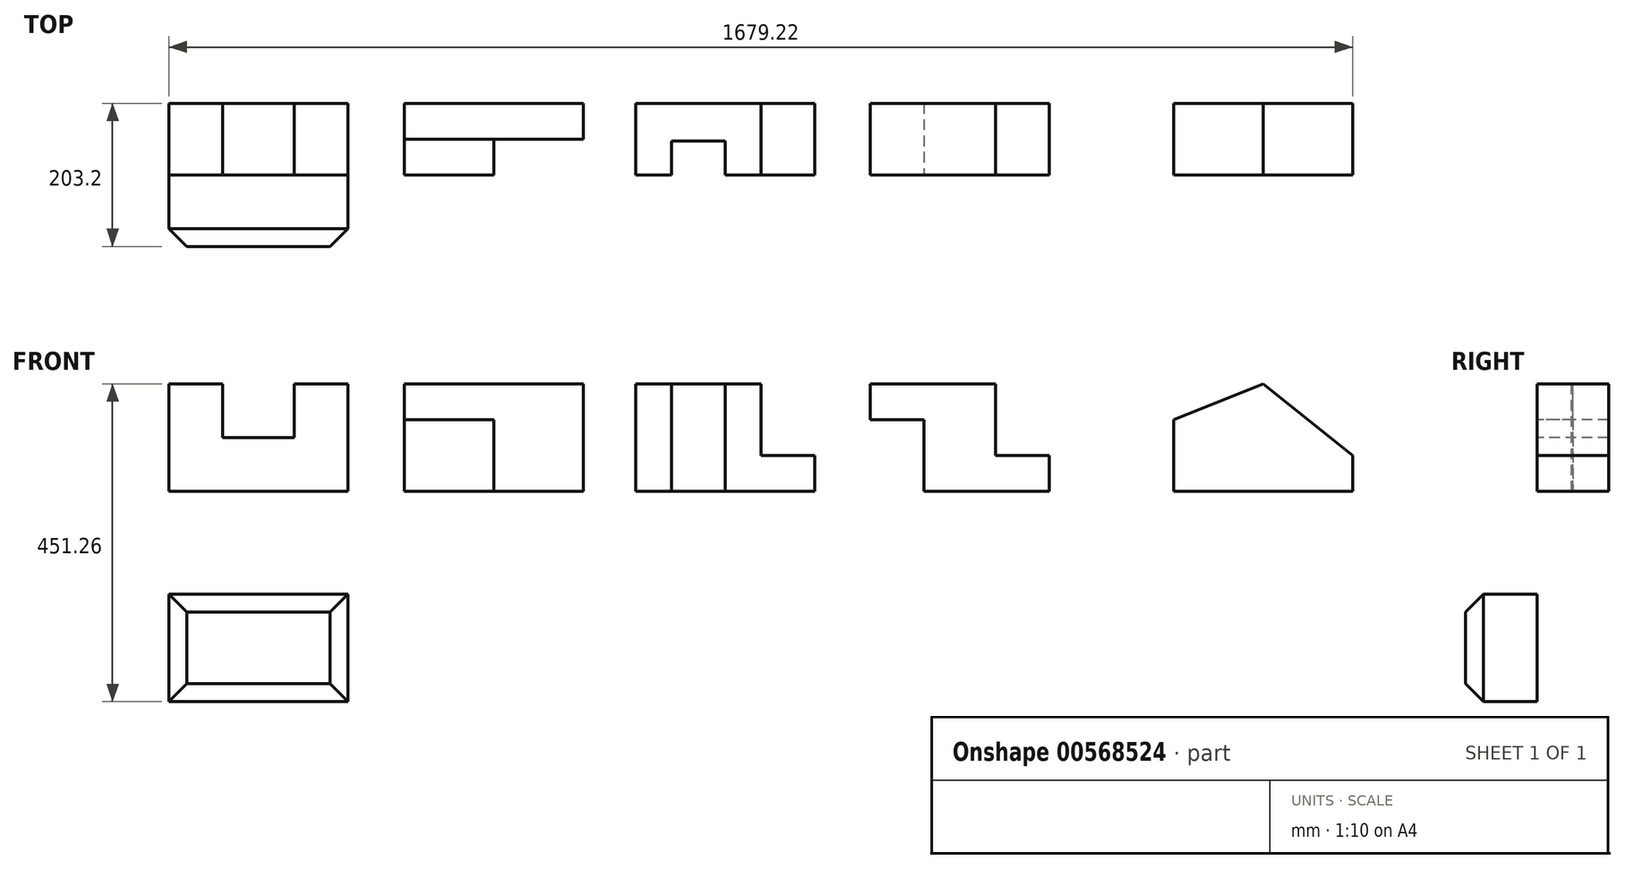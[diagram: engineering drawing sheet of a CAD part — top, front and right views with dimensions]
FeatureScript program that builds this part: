
annotation { "Feature Type Name" : "Feature", "Feature Type Description" : "" }
export const myFeature = defineFeature(function(context is Context, id is Id, definition is map)
    precondition{}
    {
        {
            var Q0;
            Q0=qCreatedBy(makeId("Front.planeOp"),FACE);
            var sketch = newSketch(context, id + "F0", { "sketchPlane" : qUnion([Q0])});
            skLineSegment(sketch, "E0", {"start": v(0, 0) * mm, "end": v(254, 0) * mm});
            skLineSegment(sketch, "E1", {"start": v(254, 0) * mm, "end": v(254, 152.4) * mm});
            skLineSegment(sketch, "E2", {"start": v(254, 152.4) * mm, "end": v(177.8, 152.4) * mm});
            skLineSegment(sketch, "E3", {"start": v(177.8, 152.4) * mm, "end": v(177.8, 76.2) * mm});
            skLineSegment(sketch, "E4", {"start": v(177.8, 76.2) * mm, "end": v(76.2, 76.2) * mm});
            skLineSegment(sketch, "E5", {"start": v(76.2, 76.2) * mm, "end": v(76.2, 152.4) * mm});
            skLineSegment(sketch, "E6", {"start": v(0, 152.4) * mm, "end": v(0, 0) * mm});
            skLineSegment(sketch, "E7", {"start": v(0, 152.4) * mm, "end": v(76.2, 152.4) * mm});
            skSolve(sketch);
        }
        {
            var Q0;
            Q0=makeQuery(id+"F0.imprint","IMPRINT",FACE,{"disambiguationData":[TD([[makeQuery(id+"F0.imprint","IMPRINT",EDGE,{"derivedFrom":sQuery(id+"F0.wireOp",EDGE,"E0")}),1.0]])]});
            extrude(context, id + "F1", {"entities" : qUnion([Q0]), "oppositeDirection" : true, "depth" : 101.6 * mm, "offsetDistance" : 25.4 * mm});
        }
        {
            var Q0;
            Q0=qCreatedBy(makeId("Front.planeOp"),FACE);
            var sketch = newSketch(context, id + "F2", { "sketchPlane" : qUnion([Q0])});
            skLineSegment(sketch, "E8.bottom", {"start": v(334.13, 0) * mm, "end": v(588.13, 0) * mm});
            skLineSegment(sketch, "E8.top", {"start": v(334.13, 152.4) * mm, "end": v(588.13, 152.4) * mm});
            skLineSegment(sketch, "E8.left", {"start": v(334.13, 0) * mm, "end": v(334.13, 152.4) * mm});
            skLineSegment(sketch, "E8.right", {"start": v(588.13, 0) * mm, "end": v(588.13, 152.4) * mm});
            skSolve(sketch);
        }
        {
            var Q0;
            Q0=makeQuery(id+"F2.imprint","IMPRINT",FACE,{"disambiguationData":[TD([[makeQuery(id+"F2.imprint","IMPRINT",EDGE,{"derivedFrom":sQuery(id+"F2.wireOp",EDGE,"E8.bottom")}),1.0]])]});
            extrude(context, id + "F3", {"entities" : qUnion([Q0]), "oppositeDirection" : true, "depth" : 101.6 * mm, "offsetDistance" : 25.4 * mm});
        }
        {
            var Q0;
            Q0=makeQuery(id+"F3.opExtrude","CAP_FACE",FACE,{"disambiguationData":[OSD([sQuery(id+"F2.wireOp",EDGE,"E8.bottom"),sQuery(id+"F2.wireOp",EDGE,"E8.top"),sQuery(id+"F2.wireOp",EDGE,"E8.left"),sQuery(id+"F2.wireOp",EDGE,"E8.right")])],"isStart":true});
            var sketch = newSketch(context, id + "F4", { "sketchPlane" : qUnion([Q0])});
            skLineSegment(sketch, "E9", {"start": v(334.13, 152.4) * mm, "end": v(334.13, 101.6) * mm});
            skLineSegment(sketch, "E10", {"start": v(334.13, 101.6) * mm, "end": v(461.13, 101.6) * mm});
            skLineSegment(sketch, "E11", {"start": v(461.13, 101.6) * mm, "end": v(461.13, 0) * mm});
            skLineSegment(sketch, "E12", {"start": v(461.13, 0) * mm, "end": v(588.13, 0) * mm});
            skLineSegment(sketch, "E13", {"start": v(588.13, 0) * mm, "end": v(588.13, 152.4) * mm});
            skLineSegment(sketch, "E14", {"start": v(588.13, 152.4) * mm, "end": v(334.13, 152.4) * mm});
            skSolve(sketch);
        }
        {
            var Q0;
            Q0=makeQuery(id+"F4.imprint","IMPRINT",FACE,{"disambiguationData":[TD([[makeQuery(id+"F4.imprint","IMPRINT",EDGE,{"derivedFrom":sQuery(id+"F4.wireOp",EDGE,"E9")}),-1.0]])]});
            extrude(context, id + "F5", {"entities" : qUnion([Q0]), "operationType" : NewBodyOperationType.REMOVE, "oppositeDirection" : true, "depth" : 50.8 * mm, "offsetDistance" : 25.4 * mm});
        }
        {
            var Q0;
            Q0=qCreatedBy(makeId("Front.planeOp"),FACE);
            var sketch = newSketch(context, id + "F6", { "sketchPlane" : qUnion([Q0])});
            skLineSegment(sketch, "E15.bottom", {"start": v(662.04, 0) * mm, "end": v(916.04, 0) * mm});
            skLineSegment(sketch, "E15.top", {"start": v(662.04, 152.4) * mm, "end": v(839.84, 152.4) * mm});
            skLineSegment(sketch, "E15.left", {"start": v(662.04, 0) * mm, "end": v(662.04, 152.4) * mm});
            skLineSegment(sketch, "E15.right", {"start": v(916.04, 0) * mm, "end": v(916.04, 50.8) * mm});
            skLineSegment(sketch, "E16", {"start": v(662.04, 152.4) * mm, "end": v(712.84, 152.4) * mm});
            skLineSegment(sketch, "E17", {"start": v(712.84, 152.4) * mm, "end": v(712.84, 0) * mm});
            skLineSegment(sketch, "E18", {"start": v(916.04, 50.8) * mm, "end": v(839.84, 50.8) * mm});
            skLineSegment(sketch, "E19", {"start": v(839.84, 50.8) * mm, "end": v(839.84, 152.4) * mm});
            skLineSegment(sketch, "E20", {"start": v(789.04, 152.4) * mm, "end": v(789.04, 0) * mm});
            skPoint(sketch, "E21.orphan", {"position": v(916.04, 152.4) * mm});
            skSolve(sketch);
        }
        {
            var Q0;
            {var subQ0=sQuery(id+"F6.wireOp",EDGE,"E15.left");Q0=makeQuery(id+"F6.imprint","IMPRINT",FACE,{"disambiguationData":[TD([[makeQuery(id+"F6.imprint","IMPRINT",EDGE,{"derivedFrom":subQ0}),-1.0]])]});}
            var Q1;
            {var subQ0=sQuery(id+"F6.wireOp",EDGE,"E17");Q1=makeQuery(id+"F6.imprint","IMPRINT",FACE,{"disambiguationData":[TD([[makeQuery(id+"F6.imprint","IMPRINT",EDGE,{"derivedFrom":subQ0}),1.0]])]});}
            var Q2;
            {var subQ0=sQuery(id+"F6.wireOp",EDGE,"E15.right");Q2=makeQuery(id+"F6.imprint","IMPRINT",FACE,{"disambiguationData":[TD([[makeQuery(id+"F6.imprint","IMPRINT",EDGE,{"derivedFrom":subQ0}),1.0]])]});}
            extrude(context, id + "F7", {"entities" : qUnion([Q0, Q1, Q2]), "oppositeDirection" : true, "depth" : 101.6 * mm, "offsetDistance" : 25.4 * mm});
        }
        {
            var Q0;
            Q0=makeQuery(id+"F7.opExtrude","CAP_FACE",FACE,{"disambiguationData":[OSD([sQuery(id+"F6.wireOp",EDGE,"E15.bottom"),sQuery(id+"F6.wireOp",EDGE,"E15.top"),sQuery(id+"F6.wireOp",EDGE,"E15.left"),sQuery(id+"F6.wireOp",EDGE,"E16"),sQuery(id+"F6.wireOp",EDGE,"E15.right"),sQuery(id+"F6.wireOp",EDGE,"E18"),sQuery(id+"F6.wireOp",EDGE,"E19")])],"isStart":true});
            var sketch = newSketch(context, id + "F8", { "sketchPlane" : qUnion([Q0])});
            skLineSegment(sketch, "E22", {"start": v(662.04, 152.4) * mm, "end": v(712.84, 152.4) * mm});
            skLineSegment(sketch, "E23", {"start": v(712.84, 152.4) * mm, "end": v(712.84, 0) * mm});
            skLineSegment(sketch, "E24", {"start": v(712.84, 152.4) * mm, "end": v(789.04, 152.4) * mm});
            skLineSegment(sketch, "E25", {"start": v(789.04, 152.4) * mm, "end": v(789.04, 0) * mm});
            skSolve(sketch);
        }
        {
            var Q0;
            {var subQ0=sQuery(id+"F8.wireOp",EDGE,"E23");Q0=makeQuery(id+"F8.imprint","IMPRINT",FACE,{"disambiguationData":[TD([[makeQuery(id+"F8.imprint","IMPRINT",EDGE,{"derivedFrom":subQ0}),1.0]])]});}
            extrude(context, id + "F9", {"entities" : qUnion([Q0]), "operationType" : NewBodyOperationType.REMOVE, "oppositeDirection" : true, "depth" : 48.26 * mm, "offsetDistance" : 25.4 * mm});
        }
        {
            var Q0;
            Q0=qCreatedBy(makeId("Front.planeOp"),FACE);
            var sketch = newSketch(context, id + "F10", { "sketchPlane" : qUnion([Q0])});
            skLineSegment(sketch, "E26.bottom", {"start": v(1071.27, 0) * mm, "end": v(1249.07, 0) * mm});
            skLineSegment(sketch, "E26.top", {"start": v(995.07, 152.4) * mm, "end": v(1172.87, 152.4) * mm});
            skLineSegment(sketch, "E26.right", {"start": v(1249.07, 0) * mm, "end": v(1249.07, 50.8) * mm});
            skLineSegment(sketch, "E27", {"start": v(995.07, 152.4) * mm, "end": v(995.07, 101.6) * mm});
            skLineSegment(sketch, "E28", {"start": v(995.07, 101.6) * mm, "end": v(1071.27, 101.6) * mm});
            skLineSegment(sketch, "E29", {"start": v(1071.27, 101.6) * mm, "end": v(1071.27, 0) * mm});
            skLineSegment(sketch, "E30", {"start": v(1249.07, 50.8) * mm, "end": v(1172.87, 50.8) * mm});
            skLineSegment(sketch, "E31", {"start": v(1172.87, 50.8) * mm, "end": v(1172.87, 152.4) * mm});
            skLineSegment(sketch, "E32", {"start": v(1172.87, 152.4) * mm, "end": v(995.07, 152.4) * mm});
            skSolve(sketch);
        }
        {
            var Q0;
            Q0=makeQuery(id+"F10.imprint","IMPRINT",FACE,{"disambiguationData":[TD([[makeQuery(id+"F10.imprint","IMPRINT",EDGE,{"derivedFrom":sQuery(id+"F10.wireOp",EDGE,"E27")}),1.0]])]});
            extrude(context, id + "F11", {"entities" : qUnion([Q0]), "oppositeDirection" : true, "depth" : 101.6 * mm, "offsetDistance" : 25.4 * mm});
        }
        {
            var Q0;
            Q0=qCreatedBy(makeId("Front.planeOp"),FACE);
            var sketch = newSketch(context, id + "F12", { "sketchPlane" : qUnion([Q0])});
            skLineSegment(sketch, "E33.bottom", {"start": v(1425.22, 0) * mm, "end": v(1679.22, 0) * mm});
            skLineSegment(sketch, "E33.left", {"start": v(1425.22, 0) * mm, "end": v(1425.22, 101.6) * mm});
            skLineSegment(sketch, "E33.right", {"start": v(1679.22, 0) * mm, "end": v(1679.22, 50.8) * mm});
            skLineSegment(sketch, "E34", {"start": v(1425.22, 101.6) * mm, "end": v(1552.22, 152.4) * mm});
            skLineSegment(sketch, "E35", {"start": v(1679.22, 50.8) * mm, "end": v(1552.22, 152.4) * mm});
            skSolve(sketch);
        }
        {
            var Q0;
            Q0=makeQuery(id+"F12.imprint","IMPRINT",FACE,{"disambiguationData":[TD([[makeQuery(id+"F12.imprint","IMPRINT",EDGE,{"derivedFrom":sQuery(id+"F12.wireOp",EDGE,"E33.bottom")}),1.0]])]});
            extrude(context, id + "F13", {"entities" : qUnion([Q0]), "oppositeDirection" : true, "depth" : 101.6 * mm, "offsetDistance" : 25.4 * mm});
        }
        {
            var Q0;
            Q0=qCreatedBy(makeId("Front.planeOp"),FACE);
            var sketch = newSketch(context, id + "F14", { "sketchPlane" : qUnion([Q0])});
            skLineSegment(sketch, "E36.bottom", {"start": v(0, -146.46) * mm, "end": v(254, -146.46) * mm});
            skLineSegment(sketch, "E36.top", {"start": v(0, -298.86) * mm, "end": v(254, -298.86) * mm});
            skLineSegment(sketch, "E36.left", {"start": v(0, -146.46) * mm, "end": v(0, -298.86) * mm});
            skLineSegment(sketch, "E36.right", {"start": v(254, -146.46) * mm, "end": v(254, -298.86) * mm});
            skSolve(sketch);
        }
        {
            var Q0;
            Q0=makeQuery(id+"F14.imprint","IMPRINT",FACE,{"disambiguationData":[TD([[makeQuery(id+"F14.imprint","IMPRINT",EDGE,{"derivedFrom":sQuery(id+"F14.wireOp",EDGE,"E36.bottom")}),-1.0]])]});
            extrude(context, id + "F15", {"entities" : qUnion([Q0]), "depth" : 101.6 * mm, "offsetDistance" : 25.4 * mm});
        }
        {
            var Q0;
            Q0=makeQuery(id+"F15.opExtrude","CAP_EDGE",EDGE,{"disambiguationData":[OSD([sQuery(id+"F14.wireOp",EDGE,"E36.right")])],"isStart":false});
            chamfer(context, id + "F16", {"entities" : qUnion([Q0]), "width" : 25.4 * mm, "tangentPropagation" : true});
        }
        {
            var Q0;
            Q0=makeQuery(id+"F15.opExtrude","CAP_EDGE",EDGE,{"disambiguationData":[OSD([sQuery(id+"F14.wireOp",EDGE,"E36.left")])],"isStart":false});
            chamfer(context, id + "F17", {"entities" : qUnion([Q0]), "width" : 25.4 * mm, "tangentPropagation" : true});
        }
        {
            var Q0;
            Q0=makeQuery(id+"F15.opExtrude","CAP_EDGE",EDGE,{"disambiguationData":[OSD([sQuery(id+"F14.wireOp",EDGE,"E36.bottom")])],"isStart":false});
            chamfer(context, id + "F18", {"entities" : qUnion([Q0]), "width" : 25.4 * mm, "tangentPropagation" : true});
        }
        {
            var Q0;
            Q0=makeQuery(id+"F15.opExtrude","CAP_EDGE",EDGE,{"disambiguationData":[OSD([sQuery(id+"F14.wireOp",EDGE,"E36.top")])],"isStart":false});
            chamfer(context, id + "F19", {"entities" : qUnion([Q0]), "width" : 25.4 * mm, "tangentPropagation" : true});
        }
    });
